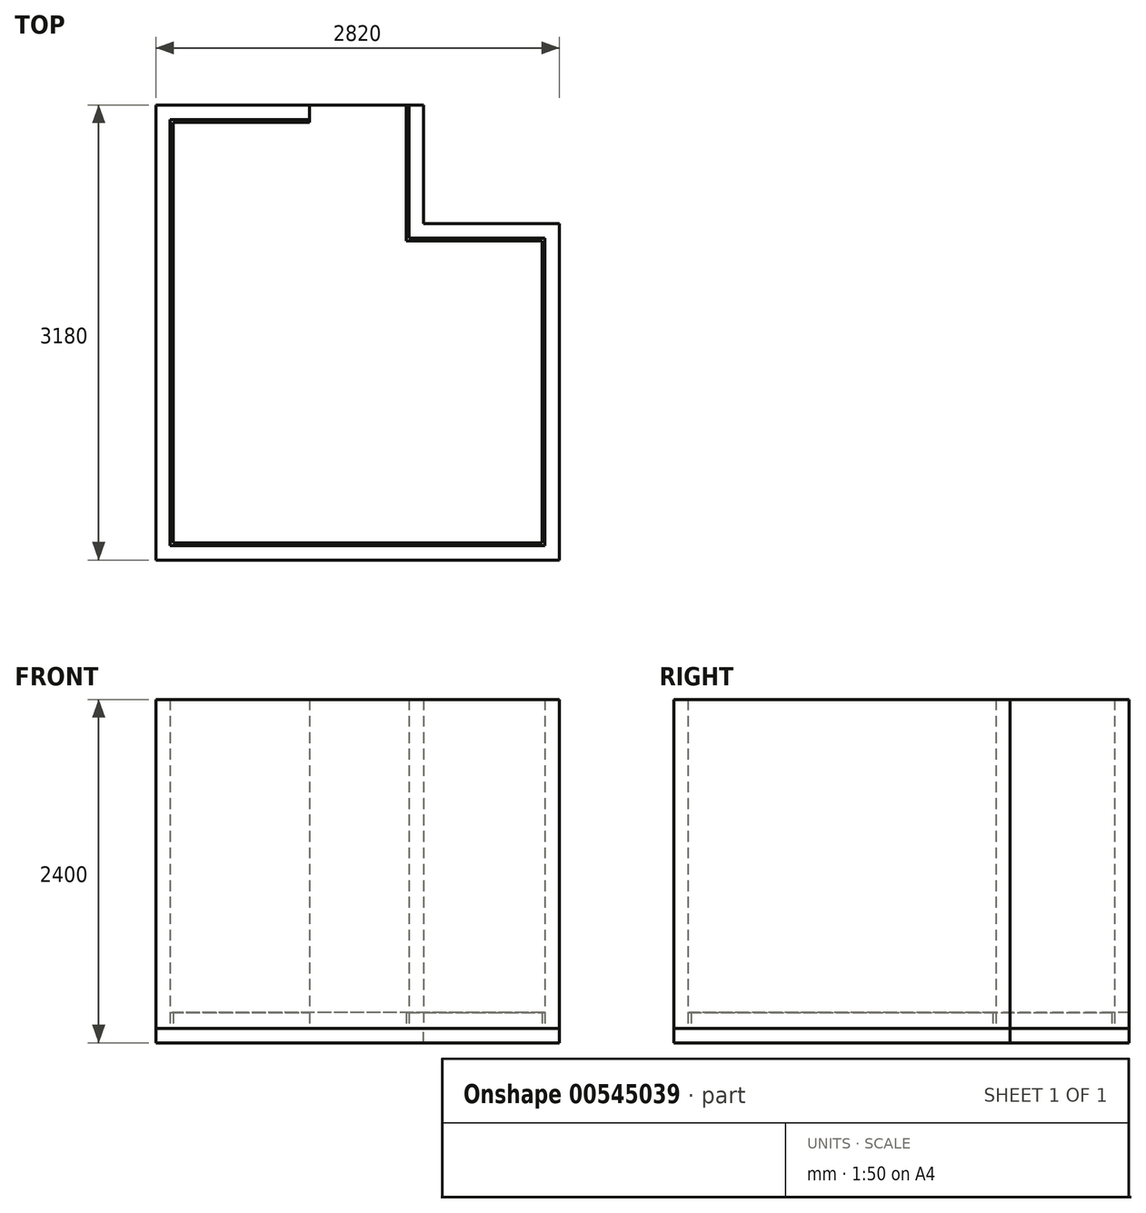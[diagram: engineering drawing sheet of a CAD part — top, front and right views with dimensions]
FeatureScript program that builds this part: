
annotation { "Feature Type Name" : "Feature", "Feature Type Description" : "" }
export const myFeature = defineFeature(function(context is Context, id is Id, definition is map)
    precondition{}
    {
        {
            var Q0;
            Q0=qCreatedBy(makeId("Top.planeOp"),FACE);
            var sketch = newSketch(context, id + "F0", { "sketchPlane" : qUnion([Q0])});
            skLineSegment(sketch, "E0", {"start": v(0, 0) * mm, "end": v(1670, 0) * mm});
            skLineSegment(sketch, "E1", {"start": v(1670, 0) * mm, "end": v(1670, -830) * mm});
            skLineSegment(sketch, "E2", {"start": v(1670, -830) * mm, "end": v(2620, -830) * mm});
            skLineSegment(sketch, "E3", {"start": v(2620, -830) * mm, "end": v(2620, -2980) * mm});
            skLineSegment(sketch, "E4", {"start": v(2620, -2980) * mm, "end": v(0, -2980) * mm});
            skLineSegment(sketch, "E5", {"start": v(0, -2980) * mm, "end": v(0, 0) * mm});
            skLineSegment(sketch, "E6.0", {"start": v(20, -2960) * mm, "end": v(20, -20) * mm});
            skLineSegment(sketch, "E6.1", {"start": v(1650, -20) * mm, "end": v(1650, -850) * mm});
            skLineSegment(sketch, "E6.2", {"start": v(1650, -850) * mm, "end": v(2600, -850) * mm});
            skLineSegment(sketch, "E6.3", {"start": v(20, -20) * mm, "end": v(1650, -20) * mm});
            skLineSegment(sketch, "E6.4", {"start": v(2600, -850) * mm, "end": v(2600, -2960) * mm});
            skLineSegment(sketch, "E6.5", {"start": v(2600, -2960) * mm, "end": v(20, -2960) * mm});
            skLineSegment(sketch, "E7.0", {"start": v(-100, -3080) * mm, "end": v(-100, 100) * mm});
            skLineSegment(sketch, "E7.1", {"start": v(1770, 100) * mm, "end": v(1770, -730) * mm});
            skLineSegment(sketch, "E7.2", {"start": v(1770, -730) * mm, "end": v(2720, -730) * mm});
            skLineSegment(sketch, "E7.3", {"start": v(-100, 100) * mm, "end": v(1770, 100) * mm});
            skLineSegment(sketch, "E7.4", {"start": v(2720, -730) * mm, "end": v(2720, -3080) * mm});
            skLineSegment(sketch, "E7.5", {"start": v(2720, -3080) * mm, "end": v(-100, -3080) * mm});
            skLineSegment(sketch, "E8", {"start": v(1670, 0) * mm, "end": v(1670, 100) * mm});
            skLineSegment(sketch, "E9", {"start": v(975, 100) * mm, "end": v(975, 0) * mm});
            skLineSegment(sketch, "E10", {"start": v(975, 0) * mm, "end": v(975, -20) * mm});
            skLineSegment(sketch, "E11", {"start": v(975, -20) * mm, "end": v(1670, -20) * mm});
            skLineSegment(sketch, "E12", {"start": v(1650, -20) * mm, "end": v(1650, 100) * mm});
            skSolve(sketch);
        }
        {
            var Q0;
            {var subQ7=sQuery(id+"F0.wireOp",EDGE,"E2");Q0=makeQuery(id+"F0.imprint","IMPRINT",FACE,{"disambiguationData":[TD([[makeQuery(id+"F0.imprint","IMPRINT",EDGE,{"derivedFrom":subQ7}),1.0]])]});}
            extrude(context, id + "F1", {"entities" : qUnion([Q0]), "depth" : 2300 * mm, "offsetDistance" : 25 * mm});
        }
        {
            var Q0;
            {var subQ4=sQuery(id+"F0.wireOp",EDGE,"E2");Q0=makeQuery(id+"F0.imprint","IMPRINT",FACE,{"disambiguationData":[TD([[makeQuery(id+"F0.imprint","IMPRINT",EDGE,{"derivedFrom":subQ4}),-1.0]])]});}
            var Q1;
            {var subQ0=sQuery(id+"F0.wireOp",EDGE,"E8");Q1=makeQuery(id+"F0.imprint","IMPRINT",FACE,{"disambiguationData":[TD([[makeQuery(id+"F0.imprint","IMPRINT",EDGE,{"derivedFrom":subQ0}),1.0]])]});}
            var Q2;
            {var subQ1=sQuery(id+"F0.wireOp",EDGE,"E0");var subQ3=sQuery(id+"F0.wireOp",EDGE,"E12");var subQ4=makeQuery(id+"F0.imprint","INTERSECT",VERTEX,{"derivedFrom":[subQ1,subQ3]});Q2=makeQuery(id+"F0.imprint","IMPRINT",FACE,{"disambiguationData":[TD([[makeQuery(id+"F0.imprint","IMPRINT",EDGE,{"disambiguationData":[TD([[subQ4,-1.0]])],"derivedFrom":subQ1}),-1.0]])]});}
            extrude(context, id + "F2", {"entities" : qUnion([Q0, Q1, Q2]), "depth" : 110 * mm, "offsetDistance" : 25 * mm});
        }
        {
            var Q0;
            Q0=makeQuery(id+"F0.imprint","IMPRINT",FACE,{"disambiguationData":[TD([[makeQuery(id+"F0.imprint","IMPRINT",EDGE,{"derivedFrom":sQuery(id+"F0.wireOp",EDGE,"E6.0")}),-1.0]])]});
            var Q1;
            {var subQ4=sQuery(id+"F0.wireOp",EDGE,"E2");Q1=makeQuery(id+"F0.imprint","IMPRINT",FACE,{"disambiguationData":[TD([[makeQuery(id+"F0.imprint","IMPRINT",EDGE,{"derivedFrom":subQ4}),1.0]])]});}
            var Q2;
            {var subQ0=sQuery(id+"F0.wireOp",EDGE,"E9");Q2=makeQuery(id+"F0.imprint","IMPRINT",FACE,{"disambiguationData":[TD([[makeQuery(id+"F0.imprint","IMPRINT",EDGE,{"derivedFrom":subQ0}),1.0]])]});}
            var Q3;
            {var subQ0=sQuery(id+"F0.wireOp",EDGE,"E8");Q3=makeQuery(id+"F0.imprint","IMPRINT",FACE,{"disambiguationData":[TD([[makeQuery(id+"F0.imprint","IMPRINT",EDGE,{"derivedFrom":subQ0}),1.0]])]});}
            var Q4;
            {var subQ1=sQuery(id+"F0.wireOp",EDGE,"E0");var subQ3=sQuery(id+"F0.wireOp",EDGE,"E12");var subQ4=makeQuery(id+"F0.imprint","INTERSECT",VERTEX,{"derivedFrom":[subQ1,subQ3]});Q4=makeQuery(id+"F0.imprint","IMPRINT",FACE,{"disambiguationData":[TD([[makeQuery(id+"F0.imprint","IMPRINT",EDGE,{"disambiguationData":[TD([[subQ4,-1.0]])],"derivedFrom":subQ1}),-1.0]])]});}
            var Q5;
            {var subQ0=sQuery(id+"F0.wireOp",EDGE,"E10");Q5=makeQuery(id+"F0.imprint","IMPRINT",FACE,{"disambiguationData":[TD([[makeQuery(id+"F0.imprint","IMPRINT",EDGE,{"derivedFrom":subQ0}),1.0]])]});}
            var Q6;
            Q6=makeQuery(id+"F2.opExtrude","CAP_FACE",FACE,{"disambiguationData":[OSD([sQuery(id+"F0.wireOp",EDGE,"E0"),sQuery(id+"F0.wireOp",EDGE,"E1"),sQuery(id+"F0.wireOp",EDGE,"E2"),sQuery(id+"F0.wireOp",EDGE,"E3"),sQuery(id+"F0.wireOp",EDGE,"E4"),sQuery(id+"F0.wireOp",EDGE,"E5"),sQuery(id+"F0.wireOp",EDGE,"E6.0"),sQuery(id+"F0.wireOp",EDGE,"E6.1"),sQuery(id+"F0.wireOp",EDGE,"E6.2"),sQuery(id+"F0.wireOp",EDGE,"E6.3"),sQuery(id+"F0.wireOp",EDGE,"E6.4"),sQuery(id+"F0.wireOp",EDGE,"E6.5"),sQuery(id+"F0.wireOp",EDGE,"E10"),sQuery(id+"F0.wireOp",EDGE,"E11")])],"isStart":false});
            var Q7;
            {var subQ4=sQuery(id+"F0.wireOp",EDGE,"E2");Q7=makeQuery(id+"F0.imprint","IMPRINT",FACE,{"disambiguationData":[TD([[makeQuery(id+"F0.imprint","IMPRINT",EDGE,{"derivedFrom":subQ4}),-1.0]])]});}
            extrude(context, id + "F3", {"entities" : qUnion([Q0, Q1, Q2, Q3, Q4, Q5, Q6, Q7]), "oppositeDirection" : true, "depth" : 100 * mm, "offsetDistance" : 25 * mm});
        }
        {
            var Q0;
            Q0=makeQuery(id+"F3.opExtrude","SWEPT_BODY",BODY,{"disambiguationData":[OSD([sQuery(id+"F0.wireOp",EDGE,"E0"),sQuery(id+"F0.wireOp",EDGE,"E1"),sQuery(id+"F0.wireOp",EDGE,"E2"),sQuery(id+"F0.wireOp",EDGE,"E3"),sQuery(id+"F0.wireOp",EDGE,"E4"),sQuery(id+"F0.wireOp",EDGE,"E5"),sQuery(id+"F0.wireOp",EDGE,"E6.0"),sQuery(id+"F0.wireOp",EDGE,"E6.1"),sQuery(id+"F0.wireOp",EDGE,"E6.2"),sQuery(id+"F0.wireOp",EDGE,"E6.3"),sQuery(id+"F0.wireOp",EDGE,"E6.4"),sQuery(id+"F0.wireOp",EDGE,"E6.5"),sQuery(id+"F0.wireOp",EDGE,"E7.3"),sQuery(id+"F0.wireOp",EDGE,"E8"),sQuery(id+"F0.wireOp",EDGE,"E10"),sQuery(id+"F0.wireOp",EDGE,"E12")])]});
            deleteBodies(context, id + "F4", {"entities" : qUnion([Q0])});
        }
    });
